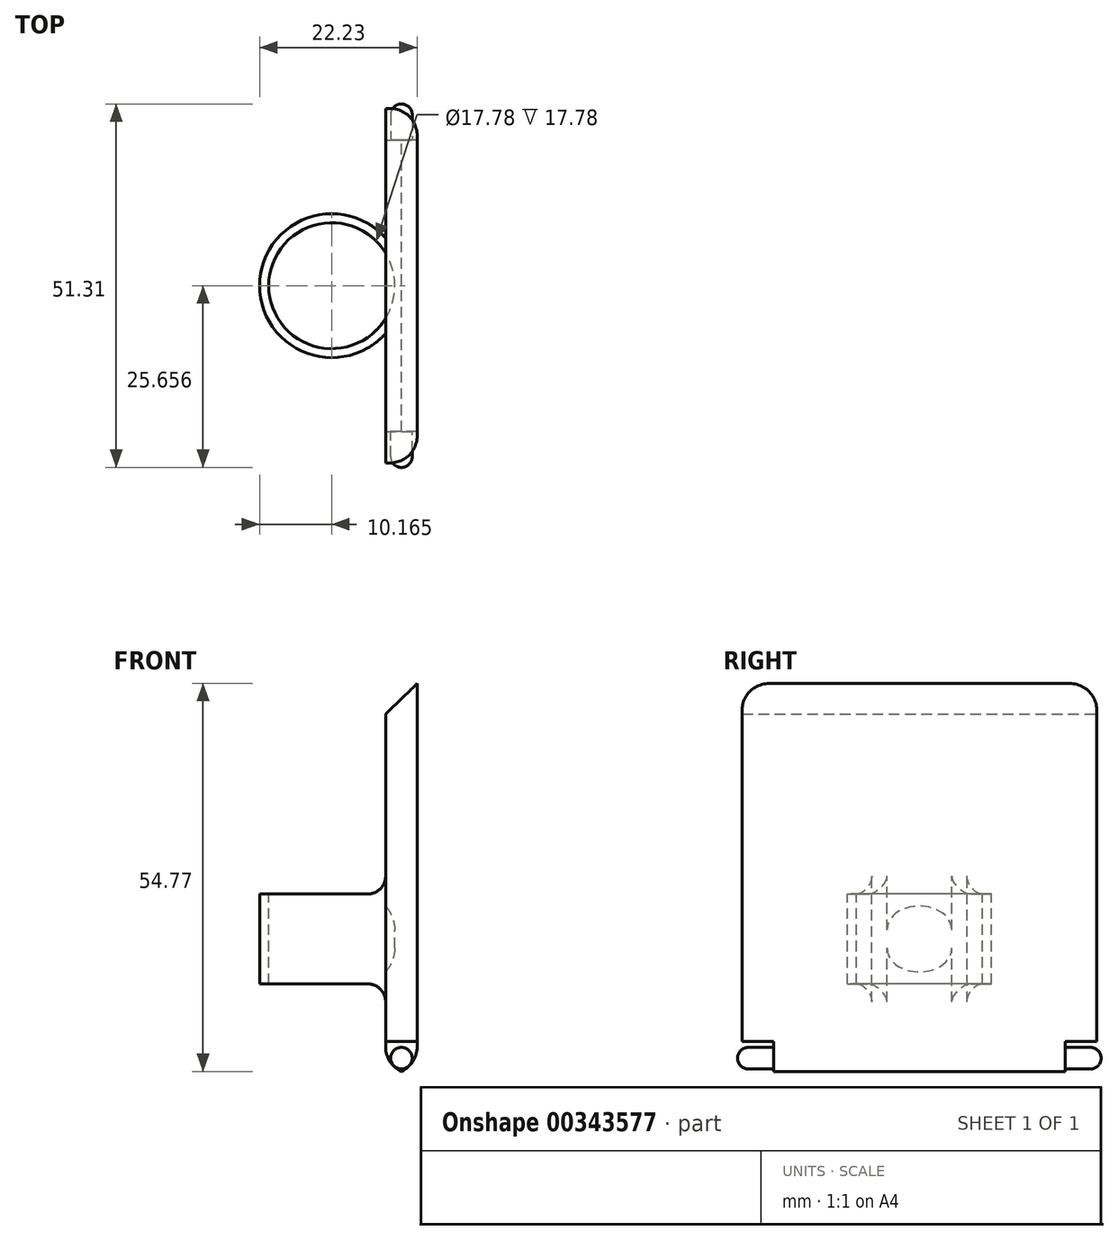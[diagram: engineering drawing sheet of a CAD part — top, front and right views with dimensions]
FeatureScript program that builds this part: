
annotation { "Feature Type Name" : "Feature", "Feature Type Description" : "" }
export const myFeature = defineFeature(function(context is Context, id is Id, definition is map)
    precondition{}
    {
        {
            var Q0;
            Q0=qCreatedBy(makeId("Front.planeOp"),FACE);
            var sketch = newSketch(context, id + "F0", { "sketchPlane" : qUnion([Q0])});
            skLineSegment(sketch, "E0.bottom", {"start": v(0, 0) * mm, "end": v(-4.45, 0) * mm});
            skLineSegment(sketch, "E0.top", {"start": v(0, 50.8) * mm, "end": v(-4.45, 50.8) * mm});
            skLineSegment(sketch, "E0.left", {"start": v(0, 0) * mm, "end": v(0, 50.8) * mm});
            skLineSegment(sketch, "E0.right", {"start": v(-4.45, 0) * mm, "end": v(-4.45, 50.8) * mm});
            skSolve(sketch);
        }
        {
            var Q0;
            Q0=qSketchRegion(id+"F0",true);
            extrude(context, id + "F1", {"entities" : qUnion([Q0]), "depth" : 41.15 * mm, "offsetDistance" : 25.4 * mm});
        }
        {
            var Q0;
            Q0=makeQuery(id+"F1.opExtrude","SWEPT_FACE",FACE,{"disambiguationData":[OSD([sQuery(id+"F0.wireOp",EDGE,"E0.right")])]});
            var sketch = newSketch(context, id + "F2", { "sketchPlane" : qUnion([Q0])});
            skLineSegment(sketch, "E1", {"start": v(41.15, 0) * mm, "end": v(41.15, 4.57) * mm});
            skLineSegment(sketch, "E2", {"start": v(41.15, 4.57) * mm, "end": v(45.6, 4.57) * mm});
            skLineSegment(sketch, "E3.bottom", {"start": v(45.6, 4.57) * mm, "end": v(41.15, 4.57) * mm});
            skLineSegment(sketch, "E3.top", {"start": v(45.6, 50.8) * mm, "end": v(41.15, 50.8) * mm});
            skLineSegment(sketch, "E3.left", {"start": v(45.6, 4.57) * mm, "end": v(45.6, 50.8) * mm});
            skLineSegment(sketch, "E3.right", {"start": v(41.15, 4.57) * mm, "end": v(41.15, 50.8) * mm});
            skSolve(sketch);
        }
        {
            var Q0;
            Q0=qSketchRegion(id+"F2",true);
            extrude(context, id + "F3", {"entities" : qUnion([Q0]), "operationType" : NewBodyOperationType.ADD, "depth" : -4.44 * mm, "offsetDistance" : 25.4 * mm});
        }
        {
            var Q0;
            Q0=makeQuery(id+"F3.boolean.opBoolean","MERGE",FACE,{"derivedFrom":[makeQuery(id+"F1.opExtrude","SWEPT_FACE",FACE,{"disambiguationData":[OSD([sQuery(id+"F0.wireOp",EDGE,"E0.right")])]}),makeQuery(id+"F3.opExtrude","CAP_FACE",FACE,{"disambiguationData":[OSD([sQuery(id+"F2.wireOp",EDGE,"E3.bottom"),sQuery(id+"F2.wireOp",EDGE,"E3.top"),sQuery(id+"F2.wireOp",EDGE,"E3.left"),sQuery(id+"F2.wireOp",EDGE,"E3.right")])],"isStart":true})]});
            var sketch = newSketch(context, id + "F4", { "sketchPlane" : qUnion([Q0])});
            skLineSegment(sketch, "E4", {"start": v(0, 0) * mm, "end": v(0, 4.57) * mm});
            skLineSegment(sketch, "E5", {"start": v(0, 4.57) * mm, "end": v(-4.45, 4.57) * mm});
            skLineSegment(sketch, "E6.bottom", {"start": v(-4.45, 4.57) * mm, "end": v(0, 4.57) * mm});
            skLineSegment(sketch, "E6.top", {"start": v(-4.44, 50.8) * mm, "end": v(0, 50.8) * mm});
            skLineSegment(sketch, "E6.left", {"start": v(-4.44, 4.57) * mm, "end": v(-4.44, 50.8) * mm});
            skLineSegment(sketch, "E6.right", {"start": v(0, 4.57) * mm, "end": v(0, 50.8) * mm});
            skSolve(sketch);
        }
        {
            var Q0;
            Q0=qSketchRegion(id+"F4",true);
            extrude(context, id + "F5", {"entities" : qUnion([Q0]), "operationType" : NewBodyOperationType.ADD, "depth" : -4.44 * mm, "offsetDistance" : 25.4 * mm});
        }
        {
            var Q0;
            Q0=makeQuery(id+"F1.opExtrude","CAP_FACE",FACE,{"disambiguationData":[OSD([sQuery(id+"F0.wireOp",EDGE,"E0.bottom"),sQuery(id+"F0.wireOp",EDGE,"E0.top"),sQuery(id+"F0.wireOp",EDGE,"E0.left"),sQuery(id+"F0.wireOp",EDGE,"E0.right")])],"isStart":true});
            var sketch = newSketch(context, id + "F6", { "sketchPlane" : qUnion([Q0])});
            skLineSegment(sketch, "E7", {"start": v(4.45, 0) * mm, "end": v(0, 0) * mm});
            skLineSegment(sketch, "E8", {"start": v(0, 0) * mm, "end": v(2.22, 0) * mm});
            skLineSegment(sketch, "E9", {"start": v(2.22, 0) * mm, "end": v(2.22, 4.45) * mm});
            skLineSegment(sketch, "E10", {"start": v(2.22, 4.45) * mm, "end": v(2.22, 2.22) * mm});
            skCircle(sketch, "E11", {"center": v(2.22, 2.22) * mm, "radius": 1.52 * mm});
            skSolve(sketch);
        }
        {
            var Q0;
            Q0=qSketchRegion(id+"F6",true);
            extrude(context, id + "F7", {"entities" : qUnion([Q0]), "operationType" : NewBodyOperationType.ADD, "depth" : 5.08 * mm, "offsetDistance" : 25.4 * mm});
        }
        {
            var Q0;
            Q0=makeQuery(id+"F1.opExtrude","CAP_FACE",FACE,{"disambiguationData":[OSD([sQuery(id+"F0.wireOp",EDGE,"E0.bottom"),sQuery(id+"F0.wireOp",EDGE,"E0.top"),sQuery(id+"F0.wireOp",EDGE,"E0.left"),sQuery(id+"F0.wireOp",EDGE,"E0.right")])],"isStart":false});
            var sketch = newSketch(context, id + "F8", { "sketchPlane" : qUnion([Q0])});
            skLineSegment(sketch, "E12", {"start": v(-4.45, 0) * mm, "end": v(0, 0) * mm});
            skLineSegment(sketch, "E13", {"start": v(0, 0) * mm, "end": v(-2.22, 0) * mm});
            skLineSegment(sketch, "E14", {"start": v(-2.22, 0) * mm, "end": v(-2.22, 4.45) * mm});
            skLineSegment(sketch, "E15", {"start": v(-2.22, 4.45) * mm, "end": v(-2.22, 2.22) * mm});
            skCircle(sketch, "E16", {"center": v(-2.22, 2.22) * mm, "radius": 1.52 * mm});
            skSolve(sketch);
        }
        {
            var Q0;
            Q0=qSketchRegion(id+"F8",true);
            extrude(context, id + "F9", {"entities" : qUnion([Q0]), "operationType" : NewBodyOperationType.ADD, "depth" : 5.08 * mm, "offsetDistance" : 25.4 * mm});
        }
        {
            var Q0;
            Q0=makeQuery(id+"F7.opExtrude","CAP_EDGE",EDGE,{"disambiguationData":[OSD([sQuery(id+"F6.wireOp",EDGE,"E11")])],"isStart":false});
            var Q1;
            Q1=makeQuery(id+"F9.opExtrude","CAP_EDGE",EDGE,{"disambiguationData":[OSD([sQuery(id+"F8.wireOp",EDGE,"E16")])],"isStart":false});
            fillet(context, id + "F10", {"entities" : qUnion([Q0, Q1]), "radius" : 1.52 * mm, "tangentPropagation" : true, "rho" : 0, "crossSection" : FilletCrossSection.CONIC, "allowEdgeOverflow" : false});
        }
        {
            var Q0;
            Q0=makeQuery(id+"F5.boolean.opBoolean","MERGE",FACE,{"derivedFrom":[makeQuery(id+"F3.boolean.opBoolean","MERGE",FACE,{"derivedFrom":[makeQuery(id+"F1.opExtrude","SWEPT_FACE",FACE,{"disambiguationData":[OSD([sQuery(id+"F0.wireOp",EDGE,"E0.top")])]}),makeQuery(id+"F3.opExtrude","SWEPT_FACE",FACE,{"disambiguationData":[OSD([sQuery(id+"F2.wireOp",EDGE,"E3.top")])]})]}),makeQuery(id+"F5.opExtrude","SWEPT_FACE",FACE,{"disambiguationData":[OSD([sQuery(id+"F4.wireOp",EDGE,"E6.top")])]})]});
            var sketch = newSketch(context, id + "F11", { "sketchPlane" : qUnion([Q0])});
            skLineSegment(sketch, "E17", {"start": v(-4.45, 4.44) * mm, "end": v(-4.45, -20.57) * mm});
            skLineSegment(sketch, "E18", {"start": v(-4.45, -20.57) * mm, "end": v(-12.07, -20.57) * mm});
            skCircle(sketch, "E19", {"center": v(-12.07, -20.57) * mm, "radius": 10.16 * mm});
            skSolve(sketch);
        }
        {
            var Q0;
            Q0 = qSketchRegion(id + "F11", true);
            extrude(context, id + "F12", {"entities" : qUnion([Q0]), "operationType" : NewBodyOperationType.ADD, "depth" : -38.1 * mm, "offsetDistance" : 25.4 * mm});
        }
        {
            var Q0;
            Q0=makeQuery(id+"F12.boolean.opBoolean","MERGE",FACE,{"derivedFrom":[makeQuery(id+"F5.boolean.opBoolean","MERGE",FACE,{"derivedFrom":[makeQuery(id+"F3.boolean.opBoolean","MERGE",FACE,{"derivedFrom":[makeQuery(id+"F1.opExtrude","SWEPT_FACE",FACE,{"disambiguationData":[OSD([sQuery(id+"F0.wireOp",EDGE,"E0.top")])]}),makeQuery(id+"F3.opExtrude","SWEPT_FACE",FACE,{"disambiguationData":[OSD([sQuery(id+"F2.wireOp",EDGE,"E3.top")])]})]}),makeQuery(id+"F5.opExtrude","SWEPT_FACE",FACE,{"disambiguationData":[OSD([sQuery(id+"F4.wireOp",EDGE,"E6.top")])]})]}),makeQuery(id+"F12.opExtrude","CAP_FACE",FACE,{"disambiguationData":[OSD([sQuery(id+"F11.wireOp",EDGE,"E19")])],"isStart":true})]});
            var sketch = newSketch(context, id + "F13", { "sketchPlane" : qUnion([Q0])});
            skCircle(sketch, "E20", {"center": v(-12.07, -20.57) * mm, "radius": 10.16 * mm});
            skLineSegment(sketch, "E21", {"start": v(-4.45, 4.44) * mm, "end": v(-4.45, -45.6) * mm});
            skSolve(sketch);
        }
        {
            var Q0;
            {var subQ0=sQuery(id+"F13.wireOp",EDGE,"E21");var subQ1=sQuery(id+"F13.wireOp",EDGE,"E20");var subQ2=makeQuery(id+"F13.imprint","INTERSECT",VERTEX,{"disambiguationData":[OD(0.0)],"derivedFrom":[subQ1,subQ0]});Q0=makeQuery(id+"F13.imprint","IMPRINT",FACE,{"disambiguationData":[TD([[makeQuery(id+"F13.imprint","IMPRINT",EDGE,{"disambiguationData":[TD([[subQ2,1.0]])],"derivedFrom":subQ1}),1.0]])]});}
            extrude(context, id + "F14", {"entities" : qUnion([Q0]), "operationType" : NewBodyOperationType.REMOVE, "oppositeDirection" : true, "depth" : 25.4 * mm, "offsetDistance" : 25.4 * mm});
        }
        {
            var Q0;
            Q0=makeQuery(id+"F14.boolean.opBoolean","COPY",FACE,{"derivedFrom":makeQuery(id+"F14.opExtrude","CAP_FACE",FACE,{"disambiguationData":[OSD([sQuery(id+"F13.wireOp",EDGE,"E20"),sQuery(id+"F13.wireOp",EDGE,"E21")])],"isStart":false})});
            var sketch = newSketch(context, id + "F15", { "sketchPlane" : qUnion([Q0])});
            skCircle(sketch, "E22", {"center": v(-12.07, -20.57) * mm, "radius": 8.9 * mm});
            skLineSegment(sketch, "E23", {"start": v(-4.45, -13.85) * mm, "end": v(-4.45, -27.3) * mm});
            skSolve(sketch);
        }
        {
            var Q0;
            Q0 = qSketchRegion(id + "F15", true);
            extrude(context, id + "F16", {"entities" : qUnion([Q0]), "operationType" : NewBodyOperationType.REMOVE, "oppositeDirection" : true, "depth" : 12.7 * mm, "offsetDistance" : 25.4 * mm});
        }
        {
            var Q0;
            {var subQ0=makeQuery(id+"F5.opExtrude","CAP_FACE",FACE,{"disambiguationData":[OSD([sQuery(id+"F4.wireOp",EDGE,"E6.bottom"),sQuery(id+"F4.wireOp",EDGE,"E6.top"),sQuery(id+"F4.wireOp",EDGE,"E6.left"),sQuery(id+"F4.wireOp",EDGE,"E6.right")])],"isStart":true});var subQ1=makeQuery(id+"F3.opExtrude","CAP_FACE",FACE,{"disambiguationData":[OSD([sQuery(id+"F2.wireOp",EDGE,"E3.bottom"),sQuery(id+"F2.wireOp",EDGE,"E3.top"),sQuery(id+"F2.wireOp",EDGE,"E3.left"),sQuery(id+"F2.wireOp",EDGE,"E3.right")])],"isStart":true});var subQ2=makeQuery(id+"F1.opExtrude","SWEPT_FACE",FACE,{"disambiguationData":[OSD([sQuery(id+"F0.wireOp",EDGE,"E0.right")])]});Q0=makeQuery(id+"F16.boolean.opBoolean","SPLIT",EDGE,{"disambiguationData":[topologyDisambiguationEdgeConnected([subQ2,subQ1,subQ0,makeQuery(id+"F14.opExtrude","SWEPT_FACE",FACE,{"disambiguationData":[OSD([sQuery(id+"F13.wireOp",EDGE,"E21")])]}),makeQuery(id+"F16.opExtrude","CAP_FACE",FACE,{"disambiguationData":[OSD([sQuery(id+"F15.wireOp",EDGE,"E22")])],"isStart":false})])],"derivedFrom":makeQuery(id+"F12.boolean.opBoolean","INTERSECT",EDGE,{"derivedFrom":[makeQuery(id+"F5.boolean.opBoolean","MERGE",FACE,{"derivedFrom":[makeQuery(id+"F3.boolean.opBoolean","MERGE",FACE,{"derivedFrom":[subQ2,subQ1]}),subQ0]}),makeQuery(id+"F12.opExtrude","CAP_FACE",FACE,{"disambiguationData":[OSD([sQuery(id+"F11.wireOp",EDGE,"E19")])],"isStart":false})]})});}
            var Q1;
            {var subQ0=sQuery(id+"F13.wireOp",EDGE,"E21");Q1=makeQuery(id+"F16.boolean.opBoolean","SPLIT",EDGE,{"disambiguationData":[topologyDisambiguationEdgeConnected([makeQuery(id+"F1.opExtrude","SWEPT_FACE",FACE,{"disambiguationData":[OSD([sQuery(id+"F0.wireOp",EDGE,"E0.right")])]}),makeQuery(id+"F3.opExtrude","CAP_FACE",FACE,{"disambiguationData":[OSD([sQuery(id+"F2.wireOp",EDGE,"E3.bottom"),sQuery(id+"F2.wireOp",EDGE,"E3.top"),sQuery(id+"F2.wireOp",EDGE,"E3.left"),sQuery(id+"F2.wireOp",EDGE,"E3.right")])],"isStart":true}),makeQuery(id+"F5.opExtrude","CAP_FACE",FACE,{"disambiguationData":[OSD([sQuery(id+"F4.wireOp",EDGE,"E6.bottom"),sQuery(id+"F4.wireOp",EDGE,"E6.top"),sQuery(id+"F4.wireOp",EDGE,"E6.left"),sQuery(id+"F4.wireOp",EDGE,"E6.right")])],"isStart":true}),makeQuery(id+"F14.opExtrude","SWEPT_FACE",FACE,{"disambiguationData":[OSD([subQ0])]}),makeQuery(id+"F16.opExtrude","CAP_FACE",FACE,{"disambiguationData":[OSD([sQuery(id+"F15.wireOp",EDGE,"E22")])],"isStart":true})])],"derivedFrom":makeQuery(id+"F14.boolean.opBoolean","COPY",EDGE,{"derivedFrom":makeQuery(id+"F14.opExtrude","CAP_EDGE",EDGE,{"disambiguationData":[OSD([subQ0])],"isStart":false})})});}
            fillet(context, id + "F17", {"entities" : qUnion([Q0, Q1]), "radius" : 2.54 * mm, "tangentPropagation" : true, "allowEdgeOverflow" : false});
        }
        {
            var Q0;
            Q0=makeQuery(id+"F5.opExtrude","SWEPT_FACE",FACE,{"disambiguationData":[OSD([sQuery(id+"F4.wireOp",EDGE,"E6.left")])]});
            var sketch = newSketch(context, id + "F18", { "sketchPlane" : qUnion([Q0])});
            skLineSegment(sketch, "E24", {"start": v(0, 50.8) * mm, "end": v(0, 55.12) * mm});
            skLineSegment(sketch, "E25", {"start": v(0, 55.12) * mm, "end": v(4.45, 50.8) * mm});
            skSolve(sketch);
        }
        {
            var Q0;
            Q0 = qSketchRegion(id + "F18", true);
            var Q1;
            Q1=makeQuery(id+"F18.imprint","IMPRINT",FACE,{"disambiguationData":[TD([[makeQuery(id+"F18.imprint","IMPRINT",EDGE,{"derivedFrom":sQuery(id+"F18.wireOp",EDGE,"2abcsXVG-dShj-Lq13-OuYG-JQ1wtrwHOAnS")}),1.0]])]});
            var Q2;
            Q2=makeQuery(id+"F18.imprint","IMPRINT",FACE,{"disambiguationData":[TD([[makeQuery(id+"F18.imprint","IMPRINT",EDGE,{"derivedFrom":sQuery(id+"F18.wireOp",EDGE,"E24")}),-1.0]])]});
            extrude(context, id + "F19", {"entities" : qUnion([Q0, Q1, Q2]), "operationType" : NewBodyOperationType.ADD, "depth" : -50.04 * mm, "offsetDistance" : 25.4 * mm});
        }
        {
            var Q0;
            Q0=makeQuery(id+"F1.opExtrude","SWEPT_EDGE",EDGE,{"disambiguationData":[OSD([sQuery(id+"F0.wireOp",EDGE,"E0.bottom"),sQuery(id+"F0.wireOp",EDGE,"E0.right")])]});
            var Q1;
            Q1=makeQuery(id+"F1.opExtrude","SWEPT_EDGE",EDGE,{"disambiguationData":[OSD([sQuery(id+"F0.wireOp",EDGE,"E0.bottom"),sQuery(id+"F0.wireOp",EDGE,"E0.left")])]});
            var Q2;
            Q2=makeQuery(id+"F19.boolean.opBoolean","MERGE",EDGE,{"derivedFrom":[makeQuery(id+"F5.opExtrude","CAP_EDGE",EDGE,{"disambiguationData":[OSD([sQuery(id+"F4.wireOp",EDGE,"E6.left")])],"isStart":false}),makeQuery(id+"F19.opExtrude","CAP_EDGE",EDGE,{"disambiguationData":[OSD([sQuery(id+"F18.wireOp",EDGE,"E24")])],"isStart":true})]});
            var Q3;
            Q3=makeQuery(id+"F19.boolean.opBoolean","MERGE",EDGE,{"derivedFrom":[makeQuery(id+"F3.opExtrude","CAP_EDGE",EDGE,{"disambiguationData":[OSD([sQuery(id+"F2.wireOp",EDGE,"E3.left")])],"isStart":false}),makeQuery(id+"F19.opExtrude","CAP_EDGE",EDGE,{"disambiguationData":[OSD([sQuery(id+"F18.wireOp",EDGE,"E24")])],"isStart":false})]});
            fillet(context, id + "F20", {"entities" : qUnion([Q0, Q1, Q2, Q3]), "radius" : 3.8 * mm, "tangentPropagation" : true, "allowEdgeOverflow" : false});
        }
        {
            var Q0;
            {var subQ0=sQuery(id+"F15.wireOp",EDGE,"E22");Q0=makeQuery(id+"F16.boolean.opBoolean","COPY",EDGE,{"disambiguationData":[topologyDisambiguationEdgeConnected([makeQuery(id+"F12.opExtrude","CAP_FACE",FACE,{"disambiguationData":[OSD([sQuery(id+"F11.wireOp",EDGE,"E19")])],"isStart":false})])],"derivedFrom":makeQuery(id+"F16.opExtrude","CAP_EDGE",EDGE,{"disambiguationData":[OSD([subQ0])],"isStart":false})});}
            var Q1;
            {var subQ0=sQuery(id+"F15.wireOp",EDGE,"E22");Q1=makeQuery(id+"F16.boolean.opBoolean","COPY",EDGE,{"disambiguationData":[topologyDisambiguationEdgeConnected([makeQuery(id+"F14.boolean.opBoolean","COPY",FACE,{"derivedFrom":makeQuery(id+"F14.opExtrude","CAP_FACE",FACE,{"disambiguationData":[OSD([sQuery(id+"F13.wireOp",EDGE,"E20"),sQuery(id+"F13.wireOp",EDGE,"E21")])],"isStart":false})})])],"derivedFrom":makeQuery(id+"F16.opExtrude","CAP_EDGE",EDGE,{"disambiguationData":[OSD([subQ0])],"isStart":true})});}
            fillet(context, id + "F21", {"entities" : qUnion([Q0, Q1]), "radius" : 5.08 * mm, "tangentPropagation" : true, "allowEdgeOverflow" : false});
        }
    });
